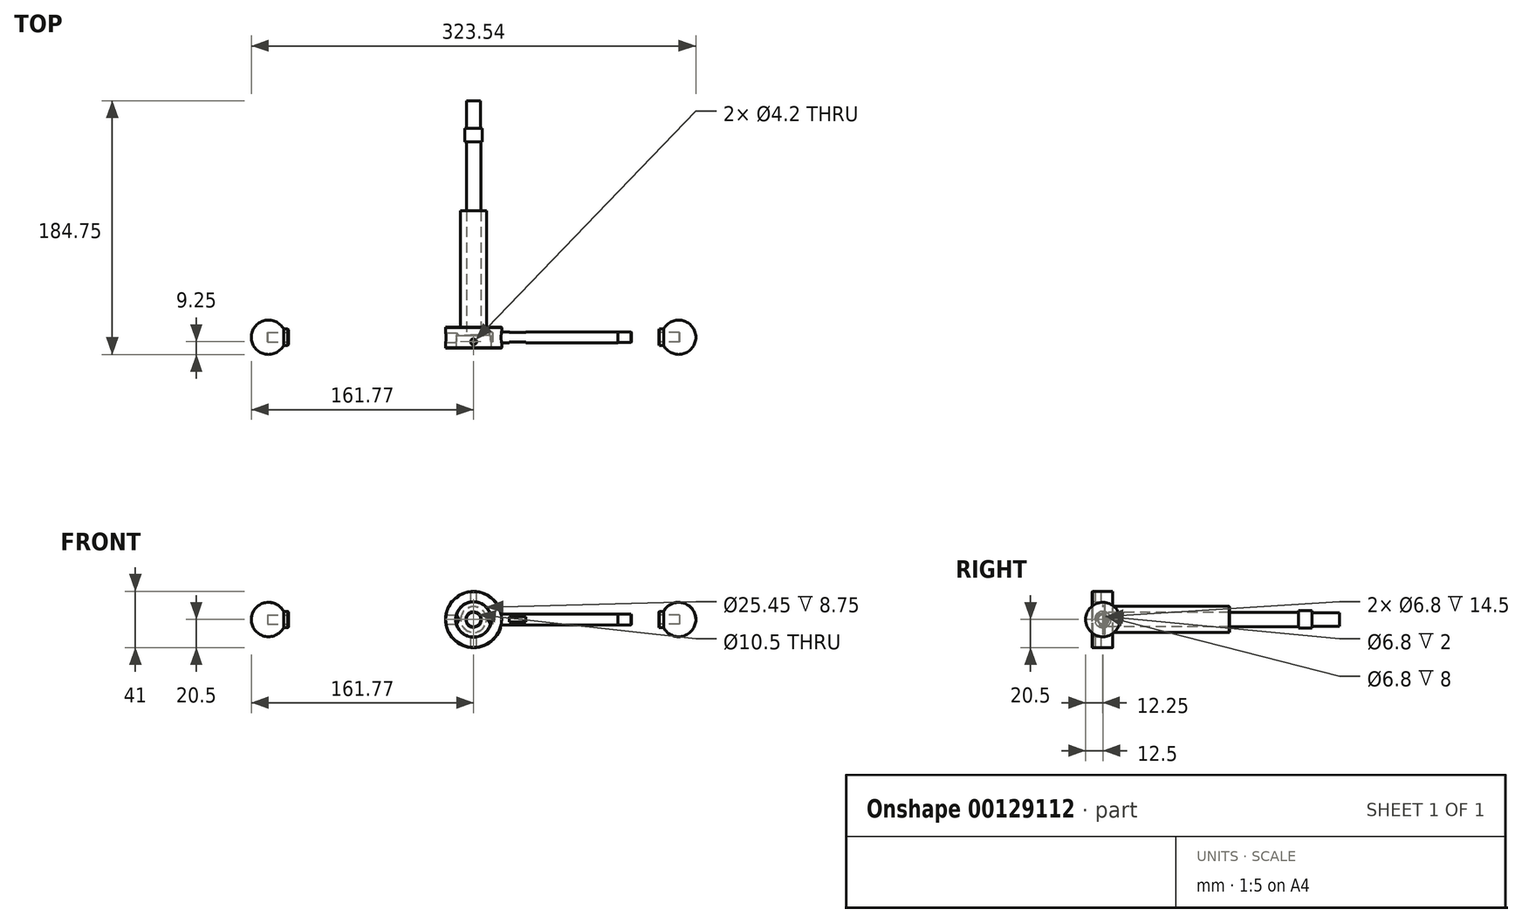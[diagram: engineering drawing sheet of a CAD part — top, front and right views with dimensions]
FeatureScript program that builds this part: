
annotation { "Feature Type Name" : "Feature", "Feature Type Description" : "" }
export const myFeature = defineFeature(function(context is Context, id is Id, definition is map)
    precondition{}
    {
        {
            var Q0;
            Q0=qCreatedBy(makeId("Front.planeOp"),FACE);
            var sketch = newSketch(context, id + "F0", { "sketchPlane" : qUnion([Q0])});
            skCircle(sketch, "E0", {"center": v(0, 0) * mm, "radius": 20.5 * mm});
            skSolve(sketch);
        }
        {
            var Q0;
            Q0=qSketchRegion(id+"F0",true);
            extrude(context, id + "F1", {"entities" : qUnion([Q0]), "oppositeDirection" : true, "depth" : 15 * mm});
        }
        {
            var Q0;
            Q0=makeQuery(id+"F1.opExtrude","CAP_FACE",FACE,{"disambiguationData":[OSD([sQuery(id+"F0.wireOp",EDGE,"E0")])],"isStart":false});
            var sketch = newSketch(context, id + "F2", { "sketchPlane" : qUnion([Q0])});
            skCircle(sketch, "E1", {"center": v(0, 0) * mm, "radius": 9.5 * mm});
            skSolve(sketch);
        }
        {
            var Q0;
            Q0=qSketchRegion(id+"F2",true);
            extrude(context, id + "F3", {"entities" : qUnion([Q0]), "operationType" : NewBodyOperationType.ADD, "depth" : 85 * mm});
        }
        {
            var Q0;
            Q0=makeQuery(id+"F1.opExtrude","CAP_FACE",FACE,{"disambiguationData":[OSD([sQuery(id+"F0.wireOp",EDGE,"E0")])],"isStart":true});
            var sketch = newSketch(context, id + "F4", { "sketchPlane" : qUnion([Q0])});
            skCircle(sketch, "E2", {"center": v(0, 0) * mm, "radius": 12.72 * mm});
            skSolve(sketch);
        }
        {
            var Q0;
            Q0=qSketchRegion(id+"F4",true);
            extrude(context, id + "F5", {"entities" : qUnion([Q0]), "operationType" : NewBodyOperationType.REMOVE, "oppositeDirection" : true, "depth" : 9 * mm});
        }
        {
            var Q0;
            Q0=makeQuery(id+"F5.boolean.opBoolean","COPY",FACE,{"derivedFrom":makeQuery(id+"F5.opExtrude","CAP_FACE",FACE,{"disambiguationData":[OSD([sQuery(id+"F4.wireOp",EDGE,"E2")])],"isStart":false})});
            var sketch = newSketch(context, id + "F6", { "sketchPlane" : qUnion([Q0])});
            skCircle(sketch, "E3", {"center": v(0, 0) * mm, "radius": 5.25 * mm});
            skSolve(sketch);
        }
        {
            var Q0;
            Q0=qSketchRegion(id+"F6",true);
            extrude(context, id + "F7", {"entities" : qUnion([Q0]), "operationType" : NewBodyOperationType.REMOVE, "endBound" : BoundingType.THROUGH_ALL, "oppositeDirection" : true, "depth" : 25 * mm});
        }
        {
            var Q0;
            Q0=makeQuery(id+"F1.opExtrude","CAP_FACE",FACE,{"disambiguationData":[OSD([sQuery(id+"F0.wireOp",EDGE,"E0")])],"isStart":true});
            var Q1;
            Q1=makeQuery(id+"F7.boolean.opBoolean","COPY",FACE,{"derivedFrom":makeQuery(id+"F7.opExtrude","SWEPT_FACE",FACE,{"disambiguationData":[OSD([sQuery(id+"F6.wireOp",EDGE,"E3")])]})});
            var Q2;
            Q2=makeQuery(id+"F1.opExtrude","SWEPT_FACE",FACE,{"disambiguationData":[OSD([sQuery(id+"F0.wireOp",EDGE,"E0")])]});
            var Q3;
            Q3=makeQuery(id+"F3.opExtrude","CAP_EDGE",EDGE,{"disambiguationData":[OSD([sQuery(id+"F2.wireOp",EDGE,"E1")])],"isStart":false});
            chamfer(context, id + "F8", {"entities" : qUnion([Q0, Q1, Q2, Q3]), "width" : .25 * mm, "tangentPropagation" : true});
        }
        {
            var Q0;
            Q0=qCreatedBy(makeId("Right.planeOp"),FACE);
            cPlane(context, id + "F9", {"entities" : qUnion([Q0]), "cplaneType" : CPlaneType.OFFSET, "offset" : (41 / 2) * mm, "width" : 150 * mm, "height" : 150 * mm});
        }
        {
            var Q0;
            Q0=qCreatedBy(id+"F9.planeOp",FACE);
            var sketch = newSketch(context, id + "F10", { "sketchPlane" : qUnion([Q0])});
            skPoint(sketch, "E4", {"position": v(7.75, 0) * mm});
            skCircle(sketch, "E5", {"center": v(7.75, 0) * mm, "radius": 4.5 * mm});
            skSolve(sketch);
        }
        {
            var Q0;
            Q0=qSketchRegion(id+"F10",true);
            extrude(context, id + "F11", {"entities" : qUnion([Q0]), "operationType" : NewBodyOperationType.REMOVE, "oppositeDirection" : true, "depth" : .5 * mm});
        }
        {
            var Q0;
            Q0=makeQuery(id+"F11.boolean.opBoolean","COPY",FACE,{"derivedFrom":makeQuery(id+"F11.opExtrude","CAP_FACE",FACE,{"disambiguationData":[OSD([sQuery(id+"F10.wireOp",EDGE,"E5")])],"isStart":false})});
            var sketch = newSketch(context, id + "F12", { "sketchPlane" : qUnion([Q0])});
            skPoint(sketch, "E6", {"position": v(7.75, 0) * mm});
            skSolve(sketch);
        }
        {
            var Q0;
            Q0=sQuery(id+"F12.wireOp",VERTEX,"E6");
            var Q1;
            Q1=makeQuery(id+"F1.opExtrude","SWEPT_BODY",BODY,{"disambiguationData":[OSD([sQuery(id+"F0.wireOp",EDGE,"E0")])]});
            hole(context, id + "F13", {"style" : HoleStyle.SIMPLE, "endStyle" : HoleEndStyle.BLIND, "holeDiameter" : 6.8 * mm, "holeDepth" : 8 * mm, "locations" : qUnion([Q0]), "scope" : qUnion([Q1])});
        }
        {
            var Q0;
            Q0=qCreatedBy(makeId("Right.planeOp"),FACE);
            cPlane(context, id + "F14", {"entities" : qUnion([Q0]), "cplaneType" : CPlaneType.OFFSET, "offset" : (41 / 2) * mm, "oppositeDirection" : true, "width" : 150 * mm, "height" : 150 * mm});
        }
        {
            var Q0;
            Q0=qCreatedBy(id+"F14.planeOp",FACE);
            var sketch = newSketch(context, id + "F15", { "sketchPlane" : qUnion([Q0])});
            skPoint(sketch, "E7", {"position": v(7.5, 0) * mm});
            skCircle(sketch, "E8", {"center": v(7.5, 0) * mm, "radius": 4.5 * mm});
            skSolve(sketch);
        }
        {
            var Q0;
            Q0=qSketchRegion(id+"F15",true);
            extrude(context, id + "F16", {"entities" : qUnion([Q0]), "operationType" : NewBodyOperationType.REMOVE, "depth" : .5 * mm});
        }
        {
            var Q0;
            Q0=makeQuery(id+"F16.boolean.opBoolean","COPY",FACE,{"derivedFrom":makeQuery(id+"F16.opExtrude","CAP_FACE",FACE,{"disambiguationData":[OSD([sQuery(id+"F15.wireOp",EDGE,"E8")])],"isStart":false})});
            var sketch = newSketch(context, id + "F17", { "sketchPlane" : qUnion([Q0])});
            skPoint(sketch, "E9", {"position": v(-7.5, 0) * mm});
            skSolve(sketch);
        }
        {
            var Q0;
            Q0=sQuery(id+"F17.wireOp",VERTEX,"E9");
            var Q1;
            Q1=makeQuery(id+"F1.opExtrude","SWEPT_BODY",BODY,{"disambiguationData":[OSD([sQuery(id+"F0.wireOp",EDGE,"E0")])]});
            hole(context, id + "F18", {"style" : HoleStyle.SIMPLE, "endStyle" : HoleEndStyle.BLIND, "holeDiameter" : 6.8 * mm, "holeDepth" : 8 * mm, "locations" : qUnion([Q0]), "scope" : qUnion([Q1])});
        }
        {
            var Q0;
            Q0=makeQuery(id+"F11.boolean.opBoolean","COPY",FACE,{"derivedFrom":makeQuery(id+"F11.opExtrude","CAP_FACE",FACE,{"disambiguationData":[OSD([sQuery(id+"F10.wireOp",EDGE,"E5")])],"isStart":false})});
            var sketch = newSketch(context, id + "F19", { "sketchPlane" : qUnion([Q0])});
            skCircle(sketch, "E10", {"center": v(7.75, 0) * mm, "radius": 3.4 * mm});
            skSolve(sketch);
        }
        {
            var Q0;
            Q0=qSketchRegion(id+"F19",true);
            extrude(context, id + "F20", {"entities" : qUnion([Q0]), "oppositeDirection" : true, "depth" : 6 * mm});
        }
        {
            var Q0;
            Q0=makeQuery(id+"F20.opExtrude","CAP_FACE",FACE,{"disambiguationData":[OSD([sQuery(id+"F19.wireOp",EDGE,"E10")])],"isStart":true});
            var sketch = newSketch(context, id + "F21", { "sketchPlane" : qUnion([Q0])});
            skCircle(sketch, "E11", {"center": v(7.75, 0) * mm, "radius": 4 * mm});
            skSolve(sketch);
        }
        {
            var Q0;
            Q0=qSketchRegion(id+"F21",true);
            extrude(context, id + "F22", {"entities" : qUnion([Q0]), "operationType" : NewBodyOperationType.ADD, "depth" : 85 * mm});
        }
        {
            var Q0;
            Q0=makeQuery(id+"F22.opExtrude","CAP_FACE",FACE,{"disambiguationData":[OSD([sQuery(id+"F21.wireOp",EDGE,"E11")])],"isStart":false});
            var sketch = newSketch(context, id + "F23", { "sketchPlane" : qUnion([Q0])});
            skCircle(sketch, "E12", {"center": v(7.75, 0) * mm, "radius": 3.9 * mm});
            skSolve(sketch);
        }
        {
            var Q0;
            Q0=qSketchRegion(id+"F23",true);
            extrude(context, id + "F24", {"entities" : qUnion([Q0]), "operationType" : NewBodyOperationType.ADD, "depth" : 10 * mm});
        }
        {
            var Q0;
            Q0=makeQuery(id+"F20.opExtrude","CAP_EDGE",EDGE,{"disambiguationData":[OSD([sQuery(id+"F19.wireOp",EDGE,"E10")])],"isStart":false});
            var Q1;
            Q1=makeQuery(id+"F24.opExtrude","CAP_EDGE",EDGE,{"disambiguationData":[OSD([sQuery(id+"F23.wireOp",EDGE,"E12")])],"isStart":false});
            chamfer(context, id + "F25", {"entities" : qUnion([Q0, Q1]), "width" : .5 * mm, "tangentPropagation" : true});
        }
        {
            var Q0;
            Q0=makeQuery(id+"F24.opExtrude","CAP_FACE",FACE,{"disambiguationData":[OSD([sQuery(id+"F23.wireOp",EDGE,"E12")])],"isStart":false});
            var sketch = newSketch(context, id + "F26", { "sketchPlane" : qUnion([Q0])});
            skPoint(sketch, "E13", {"position": v(7.75, 0) * mm});
            skSolve(sketch);
        }
        {
            var Q0;
            Q0=qCreatedBy(makeId("Front.planeOp"),FACE);
            var Q1;
            Q1=sQuery(id+"F26.wireOp",VERTEX,"E13");
            cPlane(context, id + "F27", {"entities" : qUnion([Q0, Q1]), "cplaneType" : CPlaneType.PLANE_POINT, "offset" : 25 * mm, "width" : 150 * mm, "height" : 150 * mm});
        }
        {
            var Q0;
            Q0=qCreatedBy(id+"F27.planeOp",FACE);
            var sketch = newSketch(context, id + "F28", { "sketchPlane" : qUnion([Q0])});
            skArc(sketch, "E14", {"start": v(161.77, 0) * mm, "mid": v(152.37, 12.11) * mm, "end": v(138.3, 6) * mm});
            skLineSegment(sketch, "E15", {"start": v(138.3, 6) * mm, "end": v(134.77, 6) * mm});
            skLineSegment(sketch, "E16", {"start": v(134.77, 6) * mm, "end": v(134.77, 0) * mm});
            skLineSegment(sketch, "E17", {"start": v(134.77, 0) * mm, "end": v(161.77, 0) * mm});
            skSolve(sketch);
        }
        {
            var Q0;
            Q0=qSketchRegion(id+"F28",true);
            var Q1;
            Q1=sQuery(id+"F28.wireOp",EDGE,"E17");
            revolve(context, id + "F29", {"entities" : qUnion([Q0]), "axis" : qUnion([Q1]), "revolveType" : RevolveType.FULL});
        }
        {
            var Q0;
            Q0=makeQuery(id+"F29.opRevolve","SWEPT_FACE",FACE,{"disambiguationData":[OSD([sQuery(id+"F28.wireOp",EDGE,"E16")])]});
            var sketch = newSketch(context, id + "F30", { "sketchPlane" : qUnion([Q0])});
            skCircle(sketch, "E18", {"center": v(-7.75, 0) * mm, "radius": 3.4 * mm});
            skSolve(sketch);
        }
        {
            var Q0;
            Q0=qSketchRegion(id+"F30",true);
            extrude(context, id + "F31", {"entities" : qUnion([Q0]), "operationType" : NewBodyOperationType.REMOVE, "oppositeDirection" : true, "depth" : 15 * mm});
        }
        {
            var Q0;
            Q0=makeQuery(id+"F29.opRevolve","SWEPT_FACE",FACE,{"disambiguationData":[OSD([sQuery(id+"F28.wireOp",EDGE,"E16")])]});
            chamfer(context, id + "F32", {"entities" : qUnion([Q0]), "width" : .5 * mm, "tangentPropagation" : true});
        }
        {
            var Q0;
            Q0=qCreatedBy(id+"F27.planeOp",FACE);
            cPlane(context, id + "F33", {"entities" : qUnion([Q0]), "cplaneType" : CPlaneType.OFFSET, "offset" : 4 * mm, "width" : 150 * mm, "height" : 150 * mm});
        }
        {
            var Q0;
            Q0=qCreatedBy(id+"F27.planeOp",FACE);
            cPlane(context, id + "F34", {"entities" : qUnion([Q0]), "cplaneType" : CPlaneType.OFFSET, "offset" : 4 * mm, "oppositeDirection" : true, "width" : 150 * mm, "height" : 150 * mm});
        }
        {
            var Q0;
            Q0=qCreatedBy(id+"F33.planeOp",FACE);
            var sketch = newSketch(context, id + "F35", { "sketchPlane" : qUnion([Q0])});
            skLineSegment(sketch, "E19.bottom", {"start": v(38, 4.5) * mm, "end": v(26, 4.5) * mm});
            skLineSegment(sketch, "E19.top", {"start": v(38, -4.5) * mm, "end": v(26, -4.5) * mm});
            skLineSegment(sketch, "E19.left", {"start": v(38, 4.5) * mm, "end": v(38, -4.5) * mm});
            skLineSegment(sketch, "E19.right", {"start": v(26, 4.5) * mm, "end": v(26, -4.5) * mm});
            skPoint(sketch, "E19.middle", {"position": v(32, 0) * mm});
            skSolve(sketch);
        }
        {
            var Q0;
            Q0=qSketchRegion(id+"F35",true);
            extrude(context, id + "F36", {"entities" : qUnion([Q0]), "operationType" : NewBodyOperationType.REMOVE, "oppositeDirection" : true, "depth" : .5 * mm});
        }
        {
            var Q0;
            Q0=qCreatedBy(id+"F34.planeOp",FACE);
            var sketch = newSketch(context, id + "F37", { "sketchPlane" : qUnion([Q0])});
            skLineSegment(sketch, "E20.0.0", {"start": v(38, 1.92) * mm, "end": v(26, 1.92) * mm});
            skLineSegment(sketch, "E20.0.1", {"start": v(26, 1.92) * mm, "end": v(26, -1.92) * mm});
            skLineSegment(sketch, "E20.0.2", {"start": v(26, -1.92) * mm, "end": v(38, -1.92) * mm});
            skLineSegment(sketch, "E20.0.3", {"start": v(38, -1.92) * mm, "end": v(38, 1.92) * mm});
            skSolve(sketch);
        }
        {
            var Q0;
            Q0=qSketchRegion(id+"F37",true);
            extrude(context, id + "F38", {"entities" : qUnion([Q0]), "operationType" : NewBodyOperationType.REMOVE, "depth" : .5 * mm});
        }
        {
            var Q0;
            Q0=makeQuery(id+"F20.opExtrude","SWEPT_BODY",BODY,{"disambiguationData":[OSD([sQuery(id+"F19.wireOp",EDGE,"E10")])]});
            var Q1;
            Q1=makeQuery(id+"F29.opRevolve","SWEPT_BODY",BODY,{"disambiguationData":[OSD([sQuery(id+"F28.wireOp",EDGE,"E14"),sQuery(id+"F28.wireOp",EDGE,"E15"),sQuery(id+"F28.wireOp",EDGE,"E16"),sQuery(id+"F28.wireOp",EDGE,"E17")])]});
            var Q2;
            Q2=qCreatedBy(makeId("Right.planeOp"),FACE);
            mirror(context, id + "F39", {"entities" : qUnion([Q0, Q1]), "mirrorPlane" : qUnion([Q2])});
        }
        {
            var Q0;
            Q0=qCreatedBy(makeId("Top.planeOp"),FACE);
            var sketch = newSketch(context, id + "F40", { "sketchPlane" : qUnion([Q0])});
            skCircle(sketch, "E21", {"center": v(0, 4.5) * mm, "radius": 2.1 * mm});
            skSolve(sketch);
        }
        {
            var Q0;
            Q0=qSketchRegion(id+"F40",true);
            var Q1;
            Q1=makeQuery(id+"F1.opExtrude","SWEPT_FACE",FACE,{"disambiguationData":[OSD([sQuery(id+"F0.wireOp",EDGE,"E0")])]});
            var Q2;
            Q2=makeQuery(id+"F1.opExtrude","SWEPT_FACE",FACE,{"disambiguationData":[OSD([sQuery(id+"F0.wireOp",EDGE,"E0")])]});
            extrude(context, id + "F41", {"entities" : qUnion([Q0]), "operationType" : NewBodyOperationType.REMOVE, "oppositeDirection" : true, "endBoundEntityFace" : qUnion([Q1]), "depth" : 50 * mm, "symmetric" : true});
        }
        {
            var Q0;
            Q0=makeQuery(id+"F3.opExtrude","CAP_FACE",FACE,{"disambiguationData":[OSD([sQuery(id+"F2.wireOp",EDGE,"E1")])],"isStart":false});
            var sketch = newSketch(context, id + "F42", { "sketchPlane" : qUnion([Q0])});
            skCircle(sketch, "E22", {"center": v(0, 0) * mm, "radius": 5.25 * mm});
            skSolve(sketch);
        }
        {
            var Q0;
            Q0=qSketchRegion(id+"F42",true);
            extrude(context, id + "F43", {"entities" : qUnion([Q0]), "depth" : 50 * mm});
        }
        {
            var Q0;
            Q0=makeQuery(id+"F43.opExtrude","CAP_FACE",FACE,{"disambiguationData":[OSD([sQuery(id+"F42.wireOp",EDGE,"E22")])],"isStart":false});
            var sketch = newSketch(context, id + "F44", { "sketchPlane" : qUnion([Q0])});
            skCircle(sketch, "E23", {"center": v(0, 0) * mm, "radius": 6.35 * mm});
            skSolve(sketch);
        }
        {
            var Q0;
            Q0=qSketchRegion(id+"F44",true);
            extrude(context, id + "F45", {"entities" : qUnion([Q0]), "operationType" : NewBodyOperationType.ADD, "depth" : 10 * mm});
        }
        {
            var Q0;
            Q0=makeQuery(id+"F45.opExtrude","CAP_FACE",FACE,{"disambiguationData":[OSD([sQuery(id+"F44.wireOp",EDGE,"E23")])],"isStart":false});
            var sketch = newSketch(context, id + "F46", { "sketchPlane" : qUnion([Q0])});
            skCircle(sketch, "E24", {"center": v(0, 0) * mm, "radius": 5 * mm});
            skSolve(sketch);
        }
        {
            var Q0;
            Q0=qSketchRegion(id+"F46",true);
            extrude(context, id + "F47", {"entities" : qUnion([Q0]), "operationType" : NewBodyOperationType.ADD, "depth" : 20 * mm});
        }
    });
